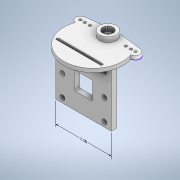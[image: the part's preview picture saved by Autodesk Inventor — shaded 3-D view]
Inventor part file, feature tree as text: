
AUTODESK INVENTOR PART (.ipt)
format: ipt  version: 2021 (Build 250183000, 183)  size: 285,184 bytes
history: native  units: in
note: dims shown in document units (in); Inventor stores cm internally (conversion verified against a paired STEP export)
features: other x4, extrude x4, sketch x4
ambient origin geometry x8: Origin, YZ Plane, XZ Plane, XY Plane, X Axis, Y Axis, Z Axis, Center Point
bodies: Solid2 (feature_tree), Solid1 (feature_tree)
feature tree (12):
  other  "Annotations"
  other  "Repaired Geometry1"
  extrude  "Extrusion1"  Depth=1.1in TaperAngle=0.0deg
  extrude  "Extrusion2"  Depth=0.02in
  extrude  "Extrusion3"  Depth=1.1in
  extrude  "Extrusion4"  Depth=1.1586in
  other  "GEOSET"
  sketch  "Sketch1"  dims[d0=0.078in d1=0.0in d2=1.1in d3=0.0in]
  sketch  "Sketch2"  dims[d4=0.02in d5=0.02in]
  sketch  "Sketch3"  dims[d6=1.1in d7=0.0in d36=0.1875in]
  sketch  "Sketch4"  dims[d37=0.1875in d40=0.1in d41=0.1in d45=0.1in d46=0.1in d47=0.1875in d48=0.1875in d49=0.02in d50=0.02in d51=1.0in d52=0.0in d10=1.1586in d8=0.3181in d9=0.3232in]
  other  "Linear Dimension 1"
